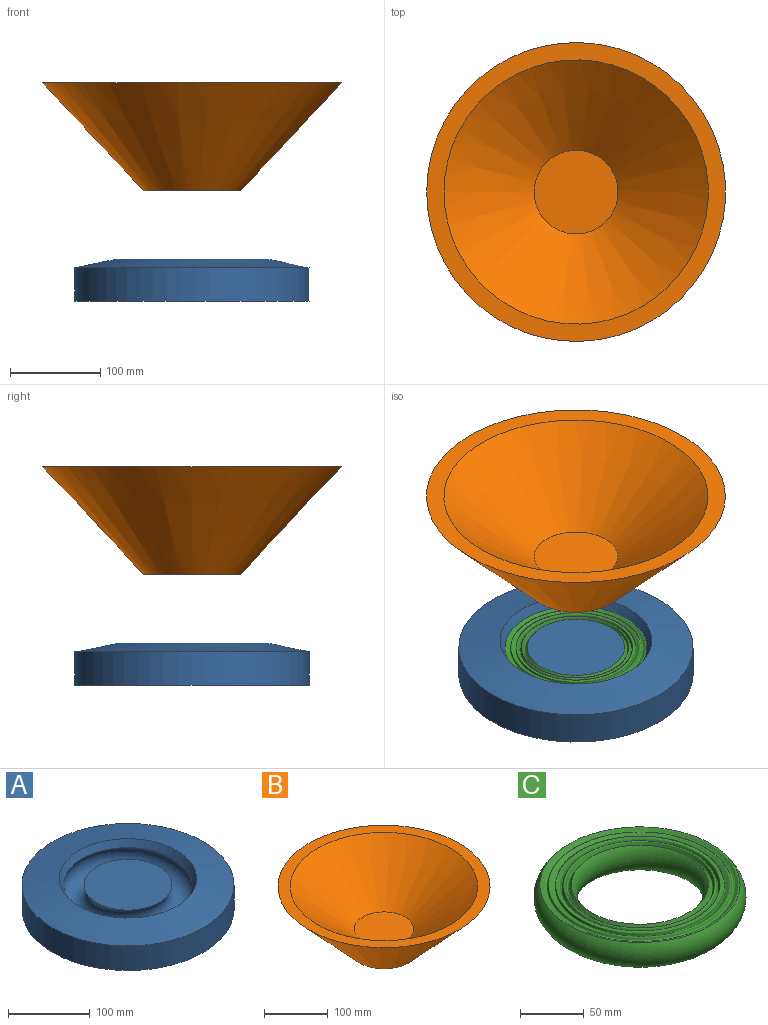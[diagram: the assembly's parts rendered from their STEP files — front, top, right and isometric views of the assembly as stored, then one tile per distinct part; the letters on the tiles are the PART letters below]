
ASSEMBLY  parts=3 mates=2
PART A: 6 faces, bbox 260x260x46.5 mm
  f0: torus R=66.37mm, axis (0,0,-1), area 33121.7mm2, adj f1,f5
  f1: plane 107.81x107.81mm, normal (0,0,1), area 9128.9mm2, adj f0
  f2: plane 259.97x259.97mm, normal (0,0,-1), area 53082.5mm2, adj f3
  f3: cylinder r=129.99mm len=259.97mm, axis (0,0,-1), area 30188.5mm2, adj f2,f4
  f4: cone r=84.26mm half-angle=78.2deg, axis (0,0,-1), area 31441.5mm2, adj f3,f5
  f5: cone r=78.84mm half-angle=29.6deg, axis (0,0,1), area 5619mm2, adj f0,f4
PART B: 5 faces, bbox 331.6x331.6x119.4 mm
  f0: cone r=46.47mm half-angle=50.9deg, axis (0,0,1), area 78264.8mm2, adj f1,f4
  f1: plane 92.95x92.95mm, normal (0,0,1), area 6785.1mm2, adj f0
  f2: plane 107.81x107.81mm, normal (0,0,-1), area 9128.9mm2, adj f3
  f3: cone r=165.8mm half-angle=43.1deg, axis (0,0,1), area 112928.3mm2, adj f2,f4
  f4: cone r=146.57mm half-angle=89.7deg, axis (0,0,1), area 18866mm2, adj f0,f3
PART C: 2 faces, bbox 180.7x180.7x29.2 mm
  f0: torus R=66.37mm, axis (0,0,-1), area 33121.7mm2, adj f1
  f1: revolved ~157.68x157.68mm, area 16455.3mm2, adj f0
PLACE A t=(-31.76,79.21,245.02)mm fixed
PLACE B t=(-31.76,79.21,330.76)mm
PLACE C t=(-31.76,79.21,245.02)mm
MATE fastened C.f0 <-> A.f0  axis (0,0,-1) through (-31.76,79.21,245.02)mm
MATE slider A.f0 <-> B.f0  axis (0,0,-1) through (-31.76,79.21,254.56)mm
